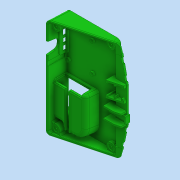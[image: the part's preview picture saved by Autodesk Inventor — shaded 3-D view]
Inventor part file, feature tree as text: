
AUTODESK INVENTOR PART (.ipt)
format: ipt  version: 2022 (Build 260153070, 153G)  size: 2,654,720 bytes
history: native  units: mm
features: other x64, plane x38, sketch x33, extrude x31, surface_op x16, fillet x15, mirror x4, revolve x4, chamfer x3, draft x3, projected_geometry x3, split x2, loft x2, thicken_offset x1, pattern_linear x1, hole x1, boolean_combine x1
ambient origin geometry x8: Origin, YZ Plane, XZ Plane, XY Plane, X Axis, Y Axis, Z Axis, Center Point
bodies: Solid4 (feature_tree)
feature tree (222):
  other  "P00173-09-002.ipt"
  other  "Blocks"
  plane  "Work Plane - Parting Line"
  plane  "Work Plane30"
  plane  "Work Plane - Front_Vent_Holes"
  plane  "Work Plane36"
  plane  "Work Plane41"
  other  "Sound_Plug_Space"
  sketch  "Sketch86"  dims[d257=30.0mm d259=15.620697mm]
  other  "Legs"
  sketch  "Sketch73"  dims[d176=10.0mm d177=0.0mm d181=0.0mm d182=90.0deg]
  sketch  "Sketch69"  dims[d157=13.962634mm d175=3.0mm]
  other  "Rim"
  sketch  "Sketch33"  dims[d115=2.274705mm]
  sketch  "Sketch30"  dims[d83=2.0mm]
  plane  "Work Plane13"
  sketch  "Sketch13"  dims[d41=20.0mm d43=49.0mm d44=20.0mm d46=58.0mm]
  sketch  "Sketch47"  dims[d119=0.0mm d120=90.0deg d121=5.0mm]
  plane  "Work Plane5"
  plane  "Work Plane10"
  other  "Connector_Box_Side"
  plane  "Work Plane6"
  sketch  "Sketch17"  dims[d60=1.5mm d61=16.0mm d62=4.0mm d63=2.0mm d64=90.0deg d65=16.75mm d66=0.0mm d81=2.0mm]
  plane  "Work Plane8"
  other  "Connector_box"
  plane  "Work Plane _Opening"
  other  "USB_Cable_Opening"
  other  "USB_Cable_Opening_Rib"
  plane  "Work Plane11"
  other  "Box_Top"
  sketch  "Sketch27"  dims[d82=2.0mm]
  other  "USB_holes"
  plane  "Work Plane34"
  other  "Power_Hole"
  sketch  "Sketch81"  dims[d93=85.0mm d96=49.0mm d97=2.8mm d98=58.0mm d99=3.5mm d133=2.0mm d135=13.2mm d136=13.2mm d142=16.0mm]
  plane  "Work Plane15"
  other  "Connector_Hole_1"
  sketch  "Sketch67"  dims[d155=5.0mm d156=13.962634mm]
  other  "Under_Con_Wall"
  plane  "Work Plane42"
  plane  "Work Plane43"
  sketch  "Sketch87"  dims[d260=14.835299mm d261=12.0mm]
  sketch  "Sketch88"  dims[d262=1.0mm d263=20.0mm d267=25.0mm]
  plane  "Work Plane19"
  sketch  "Sketch50"  dims[d122=3.5mm d123=2.5mm d137=110.0mm]
  sketch  "Sketch51"  dims[d138=5.0mm d139=5.0mm]
  plane  "Work Plane20"
  sketch  "Sketch53"  dims[d159=0.349066mm d160=3.5mm d161=1.5mm d162=3.5mm d163=16.580628mm d165=3.5mm d166=2.0mm d167=28.0mm d168=55.0mm d169=0.349066mm d170=0.349066mm d171=0.2mm d143=90.0deg]
  sketch  "Sketch52"  dims[d140=2.0mm d141=0.0mm]
  plane  "Work Plane21"
  sketch  "Sketch54"  dims[d144=90.0deg d145=5.0mm]
  plane  "Work Plane25"
  sketch  "Sketch57"  dims[d146=90.0deg d147=90.0deg]
  plane  "Work Plane26"
  sketch  "Sketch46"  dims[d116=2.274705mm d117=0.0mm d118=90.0deg]
  plane  "Work Plane32"
  plane  "Work Plane28"
  plane  "Work Plane33"
  plane  "Work Plane35"
  plane  "Work Plane37"
  sketch  "Sketch74"  dims[d183=0.0mm d184=90.0deg d185=1.0mm]
  plane  "Work Plane - Rear_Air_Hole"
  other  "Rear_Air_Hole_Strip"
  sketch  "Sketch77"  dims[d200=5.0mm d202=17.5mm d203=24.0mm d226=97.0mm d229=2.70526mm d230=10.0mm]
  sketch  "Sketch84"  dims[d100=1.2mm d101=6.93mm d102=2.98mm d109=50.0mm d110=6.0mm d111=7.0mm d246=9.0mm d256=3.5mm]
  sketch  "Sketch78"  dims[d231=66.5mm d232=4.0mm d235=2.0mm]
  plane  "Work Plane40"
  sketch  "Sketch80"  dims[d238=10.0mm d251=26.0mm]
  plane  "Work Plane39"
  sketch  "Sketch79"  dims[d236=2.0mm d237=16.0mm]
  plane  "Work Plane44"
  sketch  "Sketch91"  dims[d270=0.3mm d271=1.0mm]
  plane  "Work Plane45"
  sketch  "Sketch92"  dims[d272=2.0mm d273=2.0mm d274=3.5mm d275=3.5mm d276=1.5mm d277=0.2mm d278=3.0mm d279=3.0mm d280=2.0mm d281=10.0mm d282=-0.087266mm d283=10.0mm d284=-0.174533mm d285=22.5mm d286=0.0mm d289=7.0mm d291=7.0mm d292=5.0mm d293=12.25mm d294=0.174533mm d295=5.0mm d296=6.0mm d297=-0.174533mm d298=2.0mm d299=2.0mm d300=2.0mm d301=1.0mm d302=5.0mm d303=-0.174533mm d304=2.0mm d305=3.0mm d306=0.0mm d308=2.0mm d309=1.0mm d316=5.0mm d317=0.174533mm d318=2.0mm d319=25.0mm d320=0.0mm d321=90.0deg d322=0.0mm d323=90.0deg d326=10.0mm d327=3.0mm d328=2.0mm d335=15.0mm d336=35.75mm d337=0.0mm d340=5.0mm d341=5.0mm d343=2.0mm d371=5.0mm d372=11.75mm d373=85.0mm d374=8.75mm d375=0.0mm d376=2.0mm d377=7.5mm d378=20.0mm d379=2.0mm d380=0.0mm d383=5.862183mm d384=3.900219mm d385=1.0mm d386=1.0mm d387=5.0mm d388=20.0mm d390=12.25mm d391=3.0mm d392=0.5mm d393=2.0mm d394=60.0deg d395=15.882496mm d396=1.0mm d397=2.0mm d398=15.53343mm d399=7.0mm d400=2.0mm d401=0.0mm d402=4.0mm d403=0.0mm d404=1.0mm d405=15.882496mm d406=15.882496mm d408=3.2mm d409=4.0mm d410=-0.174533mm d411=20.0mm d412=65.0mm d413=2.274705mm d414=2.274705mm d416=15.0deg d417=8.0mm d418=8.0mm d419=14.75mm d420=0.0mm d424=25.0mm d426=2.0mm d427=2.0mm d430=15.53343mm d431=2.0mm d432=15.882496mm d433=29.0mm d438=1.0mm d439=5.0mm d440=10.0mm d441=2.0mm d442=13.0mm d443=10.0mm d444=5.0mm d445=0.174533mm d446=0.5mm d447=4.0mm d448=4.125mm d449=0.0mm d450=1.5mm d451=3.5mm d453=5.0mm d454=0.174533mm d455=1.0mm d457=5.0mm d459=2.0mm d460=65.0mm d461=15.882496mm d462=2.0mm d463=15.882496mm d464=2.0mm d467=85.0mm d468=0.174533mm d469=0.174533mm d470=2.0mm d471=15.0mm d479=1.0mm d480=1.0mm d481=1.0mm d482=15.882496mm d483=15.882496mm d484=5.25mm d485=0.0mm d493=15.882496mm d495=4.0mm d497=3.0mm d498=1.0mm d501=5.0mm d502=5.0mm d503=20.0mm d504=13.25mm d505=-0.872665mm d506=2.0mm d507=2.0mm d508=5.0mm d509=32.0mm d510=14.0mm d511=2.0mm d512=14.0mm d513=2.0mm d516=1.0mm d517=-0.872665mm d518=0.5mm d519=3.0mm d520=15.0mm d521=2.0mm d522=8.0mm d523=0.0mm d526=2.0mm d527=0.174533mm d528=0.174533mm d342=29.2mm d344=42.9mm d532=7.5mm d533=7.5mm d534=1.0mm d535=1.0mm d536=1.0mm d537=1.0mm d538=1.0mm d539=1.0mm d544=25.0mm d545=2.5mm d546=0.0mm d547=5.0mm d548=36.75mm d549=11.5mm d550=0.0mm d551=0.0mm d552=33.0mm d553=0.0mm d555=7.0mm d556=1.0mm d557=4.0mm d558=8.0mm d559=2.0mm d561=1.0mm d562=1.0mm d563=10.0mm d564=0.2mm d565=14.0mm d567=0.5mm d568=0.5mm d569=0.5mm d570=36.75mm d571=0.0mm d572=5.0mm d573=8.0mm d574=3.0mm d575=0.872665mm d580=20.0mm d581=-0.523599mm d582=45.0deg d583=10.0mm d586=7.0mm d587=1.0mm d588=7.5mm d589=1.0mm d590=3.0mm d591=1.0mm d592=2.0mm d593=1.0mm d595=3.0mm d596=3.0mm d599=3.0mm d601=101.0mm d602=101.0mm d603=1.0mm d604=1.0mm d605=5.0mm d606=3.0mm d607=0.0mm d608=0.0mm d609=3.0mm d610=2.0mm d611=75.0deg d612=3.0mm d613=2.0mm d614=75.0deg d351=0.5mm d352=0.872665mm d353=0.5mm d354=0.872665mm]
  other  "Power_Con_3"
  other  "Power_HDMI_Con"
  other  "Cable_Box"
  surface_op  "Extend2"
  mirror  "Mirror4"
  surface_op  "Stitch Surface9"
  surface_op  "Trim22"
  surface_op  "Trim23"
  surface_op  "Trim24"
  surface_op  "Trim25"
  surface_op  "Stitch Surface4"
  fillet  "Fillet16"  Radius=10.0mm
  sketch  "Sketch66"  dims[d151=69.0mm d152=0.174533mm d153=11.0mm d154=-0.174533mm]
  fillet  "Fillet12"  Radius=1.6mm
  fillet  "Fillet15"  Radius=8.0mm
  other  "Front_Vent_Holes"
  surface_op  "Extend3"
  sketch  "Sketch31"  dims[d114=5.0mm]
  surface_op  "Trim10"
  surface_op  "Trim11"
  surface_op  "Trim12"
  surface_op  "Trim13"
  surface_op  "Stitch Surface6"
  fillet  "Fillet11"  Radius=58.0mm
  thicken_offset  "Thicken4"
  extrude  "Extrusion37"  Depth=10.0mm
  extrude  "Extrusion18"  Depth=20.0mm
  extrude  "Extrusion14"  Depth=2.0mm
  mirror  "Mirror6"
  split  "Split3"
  chamfer  "Chamfer2"  Angle=90.0deg  [1 undecoded]
  extrude  "Extrusion3"  Depth=5.0mm
  pattern_linear  "Rectangular Pattern1"  Count1=11  [1 undecoded]
  hole  "Hole1"  [1 undecoded]
  extrude  "Extrusion28"  TaperAngle=90.0deg  [1 undecoded]
  boolean_combine  "Combine1"
  revolve  "Revolution1"  [1 undecoded]
  revolve  "Revolution2"  Angle=90.0deg
  split  "Split2"
  extrude  "Extrusion51"  Depth=11.0mm
  revolve  "Revolution3"  [1 undecoded]
  revolve  "Revolution4"  [1 undecoded]
  extrude  "Extrusion30"  TaperAngle=0.0deg  [1 undecoded]
  extrude  "Extrusion42"  Depth=1.0mm
  fillet  "Fillet18"  Radius=97.0mm
  fillet  "Fillet23"  Radius=2.70526mm
  fillet  "Fillet25"  Radius=10.0mm
  extrude  "Extrusion60"  Depth=4.0mm
  mirror  "Mirror1_Mount"
  fillet  "Fillet26"  Radius=2.0mm
  extrude  "Extrusion26"  Depth=16.0mm
  extrude  "Extrusion27"  Depth=26.0mm
  fillet  "Fillet14"  Radius=16.0mm
  extrude  "Extrusion23"  Depth=3.5mm
  extrude  "Extrusion24"  Depth=15.620697mm
  extrude  "Extrusion17"  Depth=12.0mm
  extrude  "Extrusion16"  Depth=25.0mm
  extrude  "Extrusion25"  Depth=2.1mm
  mirror  "Mirror3"
  extrude  "Extrusion38"  Depth=1.0mm
  extrude  "Extrusion39"  Depth=2.0mm
  extrude  "Extrusion43"  Depth=3.5mm
  fillet  "Fillet19"  Radius=3.5mm
  extrude  "Extrusion57"  Depth=1.5mm
  extrude  "Extrusion46"  Depth=0.2mm
  fillet  "Fillet21"  Radius=3.0mm
  extrude  "Extrusion49"  Depth=3.0mm
  fillet  "Fillet22"  Radius=2.0mm
  extrude  "Extrusion52"  Depth=10.0mm
  draft  "FaceDraft14"
  draft  "FaceDraft15"
  extrude  "Extrusion56"  Depth=10.0mm
  extrude  "Extrusion58"  Depth=22.5mm TaperAngle=0.0deg
  extrude  "Extrusion59"  Depth=7.0mm
  draft  "FaceDraft16"
  fillet  "Fillet27"  Radius=7.0mm
  fillet  "Fillet28"  Radius=5.0mm
  fillet  "Fillet29"  Radius=12.25mm
  extrude  "Extrusion61"  Depth=5.0mm
  chamfer  "Chamfer4"  Distance=6.0mm
  chamfer  "Chamfer5"  Distance=2.0mm
  other  "Side"
  other  "Bottom"
  plane  "Work Plane2"
  sketch  "Sketch12"  dims[d38=49.0mm d39=10.0mm d40=-0.174533mm]
  other  "PCB"
  other  "Power_HDMI_Connectors"
  other  "Srf10"
  other  "Srf12"
  other  "Srf13"
  other  "Srf14"
  other  "Srf15"
  other  "Srf16"
  other  "PCB_USB_Con"
  plane  "Work Plane11_1"
  other  "Mount_Post"
  plane  "Work Plane - Mount_Post"
  other  "Top_Housing"
  other  "Top_Housing_Bottom_Edge"
  other  "Front_USB_Lip"
  other  "USB_Position"
  other  "Srf20"
  other  "Srf21"
  plane  "Work Plane - Fan"
  other  "Fan_Top"
  other  "RPI"
  other  "USB_Ports"
  other  "Ports "
  other  "Camera_Top"
  other  "Side_Camera"
  other  "USB_Hole_Top_Cover"
  other  "Srf26"
  other  "Srf27"
  other  "Srf28"
  other  "Srf29"
  other  "Srf30"
  plane  "Work Plane - TH_Bottom_Edge"
  plane  "Work Plane31"
  other  "Srf34"
  other  "Srf35"
  other  "Srf36"
  other  "USB_Side"
  other  "Fan_Side"
  other  "Fan_Front"
  sketch  "Sketch89"  dims[d268=54.0mm]
  projected_geometry  "Projected Loop4"
  sketch  "Sketch90"  dims[d187=8.0mm d188=24.0mm d189=25.0mm d194=9.5mm d201=21.0mm d204=2.1mm]
  plane  "Work Plane - PCB_Top"
  extrude  "ExtrusionSrf14"  Depth=2.0mm
  extrude  "ExtrusionSrf13"  Depth=1.0mm
  extrude  "ExtrusionSrf11"  Depth=5.0mm
  other  "SideWalls"
  loft  "LoftSrf3"
  other  "OffsetSrf1"
  other  "Block1_1"
  loft  "LoftSrf1"
  other  "Block2:1"
  other  "Block2:2"
  other  "RPI:1"
  other  "USB_Ports:1"
  other  "Ports :2"
  other  "Camera_Top:1"
  extrude  "ExtrusionSrf12"  Depth=2.0mm
  projected_geometry  "Project Cut Edges1"
  projected_geometry  "Project Cut Edges2"
  surface_op  "Boundary Patch9"
  surface_op  "Boundary Patch1"
  surface_op  "Boundary Patch2"
note: 8 required parameter values undecoded (feature->parameter linkage not recoverable at this tier; creation-order binding heuristic only, values carry confidence <= 0.55)